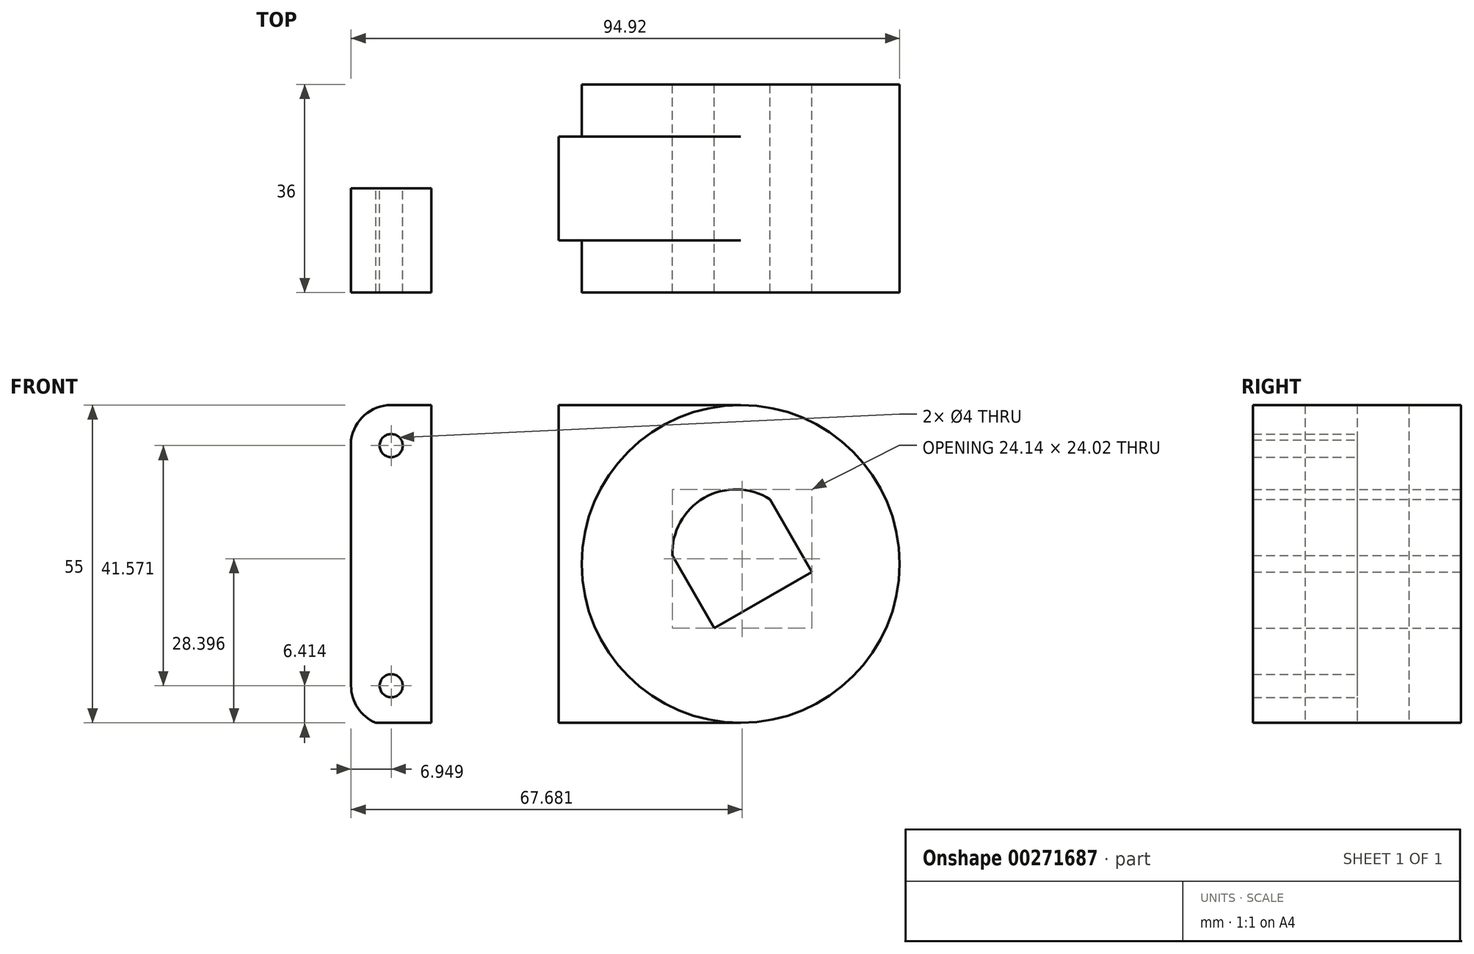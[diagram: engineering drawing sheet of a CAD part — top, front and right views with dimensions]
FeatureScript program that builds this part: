
annotation { "Feature Type Name" : "Feature", "Feature Type Description" : "" }
export const myFeature = defineFeature(function(context is Context, id is Id, definition is map)
    precondition{}
    {
        {
            var Q0;
            Q0=qCreatedBy(makeId("Front.planeOp"),FACE);
            var sketch = newSketch(context, id + "F0", { "sketchPlane" : qUnion([Q0])});
            skPoint(sketch, "E0.middle", {"position": v(1.75, -0.14) * mm});
            skArc(sketch, "E1", {"start": v(44.26, 27.36) * mm, "mid": v(71.76, -0.14) * mm, "end": v(44.26, -27.64) * mm});
            skLineSegment(sketch, "E2.top", {"start": v(56.59, -1.5) * mm, "end": v(39.7, -11.25) * mm});
            skLineSegment(sketch, "E2.left", {"start": v(49.34, 11.05) * mm, "end": v(56.59, -1.5) * mm});
            skLineSegment(sketch, "E2.right", {"start": v(32.45, 1.3) * mm, "end": v(39.7, -11.25) * mm});
            skPoint(sketch, "E2.middle", {"position": v(44.35, -0.12) * mm});
            skArc(sketch, "E3", {"start": v(49.34, 11.05) * mm, "mid": v(37.94, 11.3) * mm, "end": v(32.45, 1.3) * mm});
            skLineSegment(sketch, "E4", {"start": v(-9.27, 27.36) * mm, "end": v(-9.27, -27.64) * mm});
            skLineSegment(sketch, "E5.bottom", {"start": v(44.26, 27.36) * mm, "end": v(12.76, 27.36) * mm});
            skLineSegment(sketch, "E5.top", {"start": v(44.26, -27.64) * mm, "end": v(12.76, -27.64) * mm});
            skLineSegment(sketch, "E5.right", {"start": v(12.76, 27.36) * mm, "end": v(12.76, -27.64) * mm});
            skPoint(sketch, "E6", {"position": v(-16.21, 20.34) * mm});
            skPoint(sketch, "E7", {"position": v(-16.21, -21.23) * mm});
            skLineSegment(sketch, "E8", {"start": v(-23.16, 27.36) * mm, "end": v(-23.16, -27.64) * mm});
            skLineSegment(sketch, "E9", {"start": v(-9.27, 27.36) * mm, "end": v(-23.16, 27.36) * mm});
            skLineSegment(sketch, "E10", {"start": v(-23.16, -27.64) * mm, "end": v(-9.27, -27.64) * mm});
            skCircle(sketch, "E11", {"center": v(44.26, -0.14) * mm, "radius": 27.5 * mm});
            skPoint(sketch, "E11.second.point", {"position": v(70.45, 8.27) * mm});
            skArc(sketch, "E12", {"start": v(-16.21, 27.36) * mm, "mid": v(-20.8, 25.65) * mm, "end": v(-23.16, 21.35) * mm});
            skArc(sketch, "E13", {"start": v(-23.16, -21.23) * mm, "mid": v(-21.99, -25.08) * mm, "end": v(-18.88, -27.64) * mm});
            skSolve(sketch);
        }
        {
            var Q0;
            Q0=makeQuery(id+"F0.imprint","IMPRINT",FACE,{"disambiguationData":[TD([[makeQuery(id+"F0.imprint","IMPRINT",EDGE,{"derivedFrom":sQuery(id+"F0.wireOp",EDGE,"E4")}),-1.0]])]});
            extrude(context, id + "F1", {"entities" : qUnion([Q0]), "depth" : 18 * mm});
        }
        {
            var Q0;
            Q0=sQuery(id+"F0.wireOp",VERTEX,"E6");
            var Q1;
            Q1=sQuery(id+"F0.wireOp",VERTEX,"E7");
            var Q2;
            Q2=makeQuery(id+"F1.opExtrude","SWEPT_BODY",BODY,{"disambiguationData":[OSD([sQuery(id+"F0.wireOp",EDGE,"E4"),sQuery(id+"F0.wireOp",EDGE,"E8"),sQuery(id+"F0.wireOp",EDGE,"E9"),sQuery(id+"F0.wireOp",EDGE,"E10")])]});
            hole(context, id + "F2", {"style" : HoleStyle.SIMPLE, "endStyle" : HoleEndStyle.THROUGH, "oppositeDirection" : true, "holeDiameter" : 4 * mm, "tappedDepth" : 12 * mm, "tapClearance" : 3, "locations" : qUnion([Q0, Q1]), "scope" : qUnion([Q2])});
        }
        {
            var Q0;
            Q0=makeQuery(id+"F0.imprint","IMPRINT",FACE,{"disambiguationData":[TD([[makeQuery(id+"F0.imprint","IMPRINT",EDGE,{"derivedFrom":sQuery(id+"F0.wireOp",EDGE,"E2.top")}),1.0]])]});
            extrude(context, id + "F3", {"entities" : qUnion([Q0]), "depth" : 18 * mm, "hasSecondDirection" : true, "secondDirectionOppositeDirection" : true, "secondDirectionDepth" : 18 * mm});
        }
        {
            var Q0;
            {var subQ0=sQuery(id+"F0.wireOp",EDGE,"E5.bottom");Q0=makeQuery(id+"F0.imprint","IMPRINT",FACE,{"disambiguationData":[TD([[makeQuery(id+"F0.imprint","IMPRINT",EDGE,{"derivedFrom":subQ0}),1.0]])]});}
            extrude(context, id + "F4", {"entities" : qUnion([Q0]), "operationType" : NewBodyOperationType.ADD, "depth" : 9 * mm, "hasSecondDirection" : true, "secondDirectionOppositeDirection" : true, "secondDirectionDepth" : 9 * mm});
        }
    });
